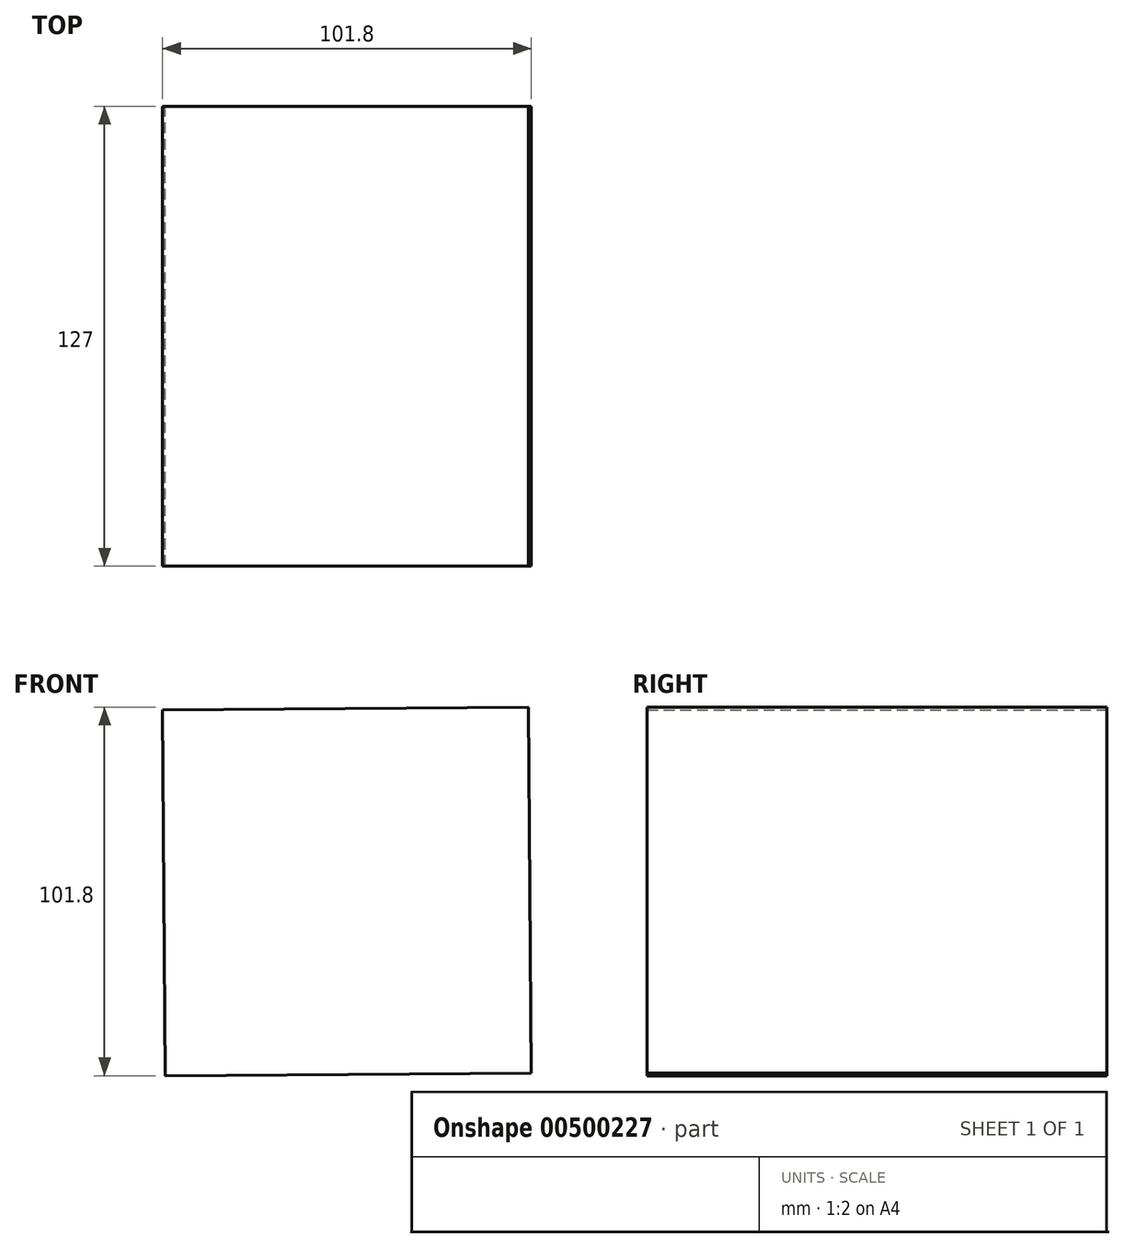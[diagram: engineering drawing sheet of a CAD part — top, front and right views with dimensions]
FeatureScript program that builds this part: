
annotation { "Feature Type Name" : "Feature", "Feature Type Description" : "" }
export const myFeature = defineFeature(function(context is Context, id is Id, definition is map)
    precondition{}
    {
        {
            var Q0;
            Q0=qCreatedBy(makeId("Front.planeOp"),FACE);
            var sketch = newSketch(context, id + "F0", { "sketchPlane" : qUnion([Q0])});
            skCircle(sketch, "E0.cCircle", {"center": v(0, 0) * mm, "radius": 71.47 * mm, "construction": true});
            skLineSegment(sketch, "E0.0", {"start": v(50.9, -50.16) * mm, "end": v(-50.16, -50.9) * mm});
            skLineSegment(sketch, "E0.1", {"start": v(-50.16, -50.9) * mm, "end": v(-50.9, 50.16) * mm});
            skLineSegment(sketch, "E0.2", {"start": v(-50.9, 50.16) * mm, "end": v(50.16, 50.9) * mm});
            skLineSegment(sketch, "E0.3", {"start": v(50.16, 50.9) * mm, "end": v(50.9, -50.16) * mm});
            skSolve(sketch);
        }
        {
            var Q0;
            Q0 = qSketchRegion(id + "F0", true);
            extrude(context, id + "F1", {"entities" : qUnion([Q0]), "depth" : 127 * mm});
        }
    });
